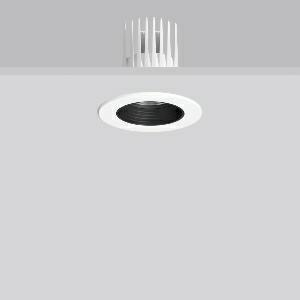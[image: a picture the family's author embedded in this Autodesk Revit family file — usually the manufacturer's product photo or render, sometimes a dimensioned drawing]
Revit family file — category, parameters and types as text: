
# Revit family: heledon_mini_e_901747_002_2_76_0bde
name_source: partatom
category: Lighting Fixtures
units: mm (PartAtom-declared; Revit-internal decimal feet)

## family parameters
Cut with Voids When Loaded = No
Host = Face
Light Source = No
Part Type = Normal
Room Calculation Point = No
Round Connector Dimension = Use Diameter
Shared = No

## types (1)
- HELEDON mini E (1 x LED Modul 927, 1850 lm, 2700)
    Apparent Load = 20 VA
    Approval mark = CE
    CIE Flux Codes = 95 100 100 100 100
    Color Rendering = 92
    Color Temperature = 2700
    Default Elevation = 1800 mm
    Description = Series: HELEDON mini
Round recessed downlight. Housing: die-cast aluminium, powder-coated. Black plastic ring and recessed LED to prevent glare from the side. Optical assembly with lens made of plastic (polycarbonate) for the best homogeneous light distribution - can be changed without tools. Best colour rendering index Ra>90. Suitable for Recessed ceiling mounting. Installation without tools thanks to spring fastening system. Including separate LED converter with connecting cable 600 mm.High quality converter without flickering and stroboscopic effect. Through-wiring box (5 pole) available as accessory. The following accessories can be mounted without use of tools: interchangeable lenses, decorative glasses, honeycomb louvre, clear and frosted diffusers, white interchangeable plastic ring. 
Colour: traffic white, matt (RAL 9016)
Diameter: 124 mm
Height: 3 mm
Cut-out diameter: 114 mm
Recess height: 170 mm
Luminaire: recess height: 120 mm
Lamp: LED
Socket: without socket
Colour temperature: 2700K
Colour rendering index (CRI): 92
System power: 20 W
Rated luminous flux: 1850 lm
Luminous efficiency: 93 lm/W
Control gear: Converter, dimmable, DALI
Protection class: II
Type of protection: IP 20
    Height = 0 mm  [stored 0 ft]
    Lamp = 1 x LED Modul 927
    Lamp Light Flux = 1850 lm
    Lamp count = 1
    Length = 124 mm  [stored 0.406824 ft]
    Lifetime = 50000 h
    Luminous efficacy = 93 lm/W
    Manufacturer = RZB
    ModVariant = No
    Model = 901747.002.2.76
    Mounting Place = Ceiling
    Mounting Type = Recessed
    Number of Poles = 1
    OnlyDefault = Yes
    Power Factor = 1
    Product Name = HELEDON mini E
    Product group = Recessed downlights
    ProductGroupID = 402
    Protection Class = Protection class II
    Protection Degree = IP 20
    RLX_Detail_Level = 1
    RLX_Emergency_Light_Flux = 0 lm
    RLX_Emergency_Type = 0
    RLX_Emergency_Type_DB = No
    RlxData = <blob elided: 132253 chars, md5=71871b61>
    Socket = socket
    Standby Power = 0 W
    System Light Flux = 1850 lm
    System Power = 20 W
    Type Comments = Product without accessories
    Type Image = 901656.002.jpg
    URL = http://relux.com
    VarID = ---
    Voltage = 230 V
    Voltage Range = 220-240 V
    Weight = 0.00 kg
    Width = 0 mm  [stored 0 ft]

note: [stored X ft] marks values corroborated as IEEE doubles in the binary element streams (Revit-internal decimal feet)

## geometry (parser evidence)
native form markers: Blend x4, Sweep x10
no freeform markers — native parametric forms only
